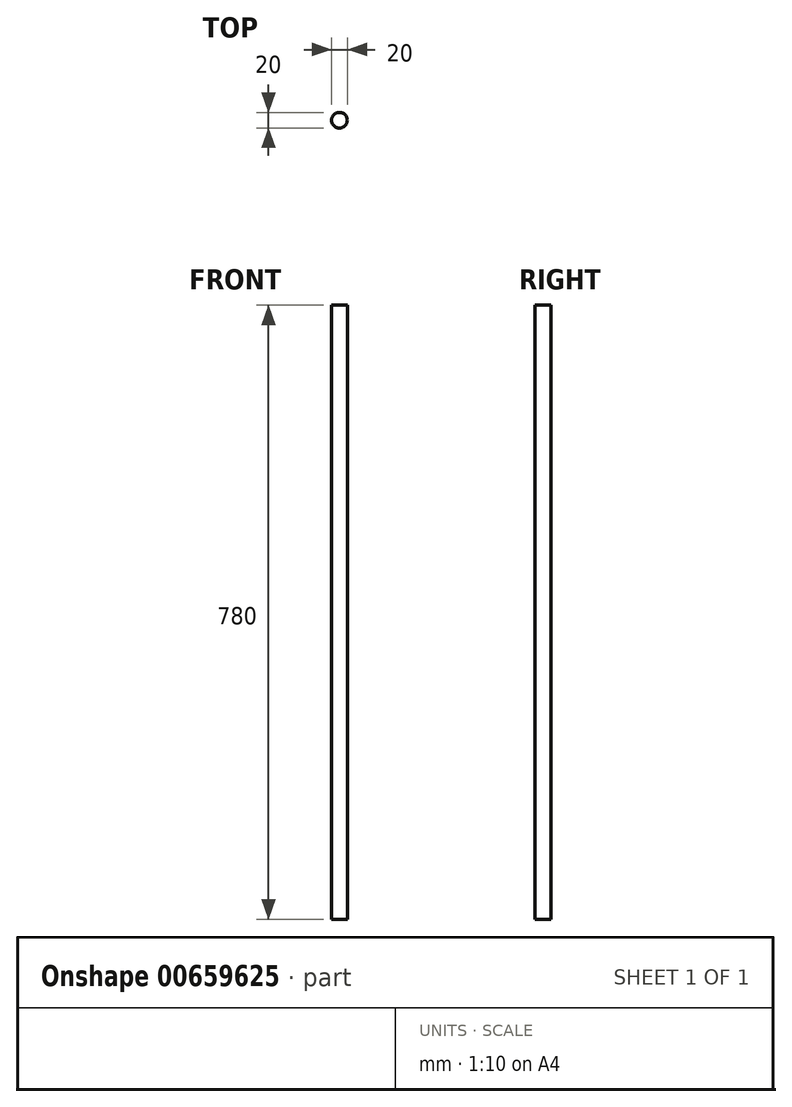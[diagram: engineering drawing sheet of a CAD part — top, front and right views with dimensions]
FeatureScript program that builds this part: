
annotation { "Feature Type Name" : "Feature", "Feature Type Description" : "" }
export const myFeature = defineFeature(function(context is Context, id is Id, definition is map)
    precondition{}
    {
        {
            var Q0;
            Q0=qCreatedBy(makeId("Top.planeOp"),FACE);
            var sketch = newSketch(context, id + "F0", { "sketchPlane" : qUnion([Q0])});
            skCircle(sketch, "E0", {"center": v(0, 0) * mm, "radius": 10 * mm});
            skSolve(sketch);
        }
        {
            var Q0;
            Q0 = qSketchRegion(id + "F0", true);
            extrude(context, id + "F1", {"entities" : qUnion([Q0]), "depth" : 780 * mm, "offsetDistance" : 25 * mm});
        }
    });
